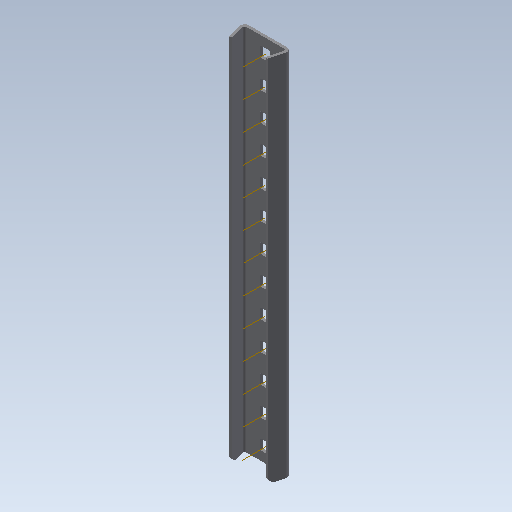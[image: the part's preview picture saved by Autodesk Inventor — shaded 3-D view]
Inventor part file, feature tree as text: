
AUTODESK INVENTOR PART (.ipt)
format: ipt  version: 2020 (Build 240168000, 168)  size: 425,472 bytes
history: native  units: in
note: dims shown in document units (in); Inventor stores cm internally (conversion verified against a paired STEP export)
features: other x17, boolean_combine x1, extrude x1, pattern_linear x1, imported_body x1, sketch x1
ambient origin geometry x8: Origin, YZ Plane, XZ Plane, XY Plane, X Axis, Y Axis, Z Axis, Center Point
bodies: Body1 (feature_tree)
feature tree (22):
  boolean_combine  "Combine1"
  other  "Linear Slide"
  other  "Work Axis1"
  extrude  "Extrusion1"  TaperAngle=0.0deg  [1 undecoded]
  pattern_linear  "Rectangular Pattern1"  Spacing1=0.0in  [1 undecoded]
  other  "bottom plane"
  other  "top plane"
  imported_body  "Base1"
  other  "Work Point1"
  other  "Work Axis2"
  sketch  "Sketch1"  dims[d0=5.1181in d2=0.5in d4=0.0in d5=0.0in d6=0.0in d8=0.0in]
  other  "Work Axis46"
  other  "Work Axis47"
  other  "Work Axis48"
  other  "Work Axis49"
  other  "Work Axis50"
  other  "Work Axis51"
  other  "Work Axis52"
  other  "Work Axis102"
  other  "Work Axis103"
  other  "Work Axis104"
  other  "Work Axis105"
note: 2 required parameter values undecoded (feature->parameter linkage not recoverable at this tier; creation-order binding heuristic only, values carry confidence <= 0.55)
